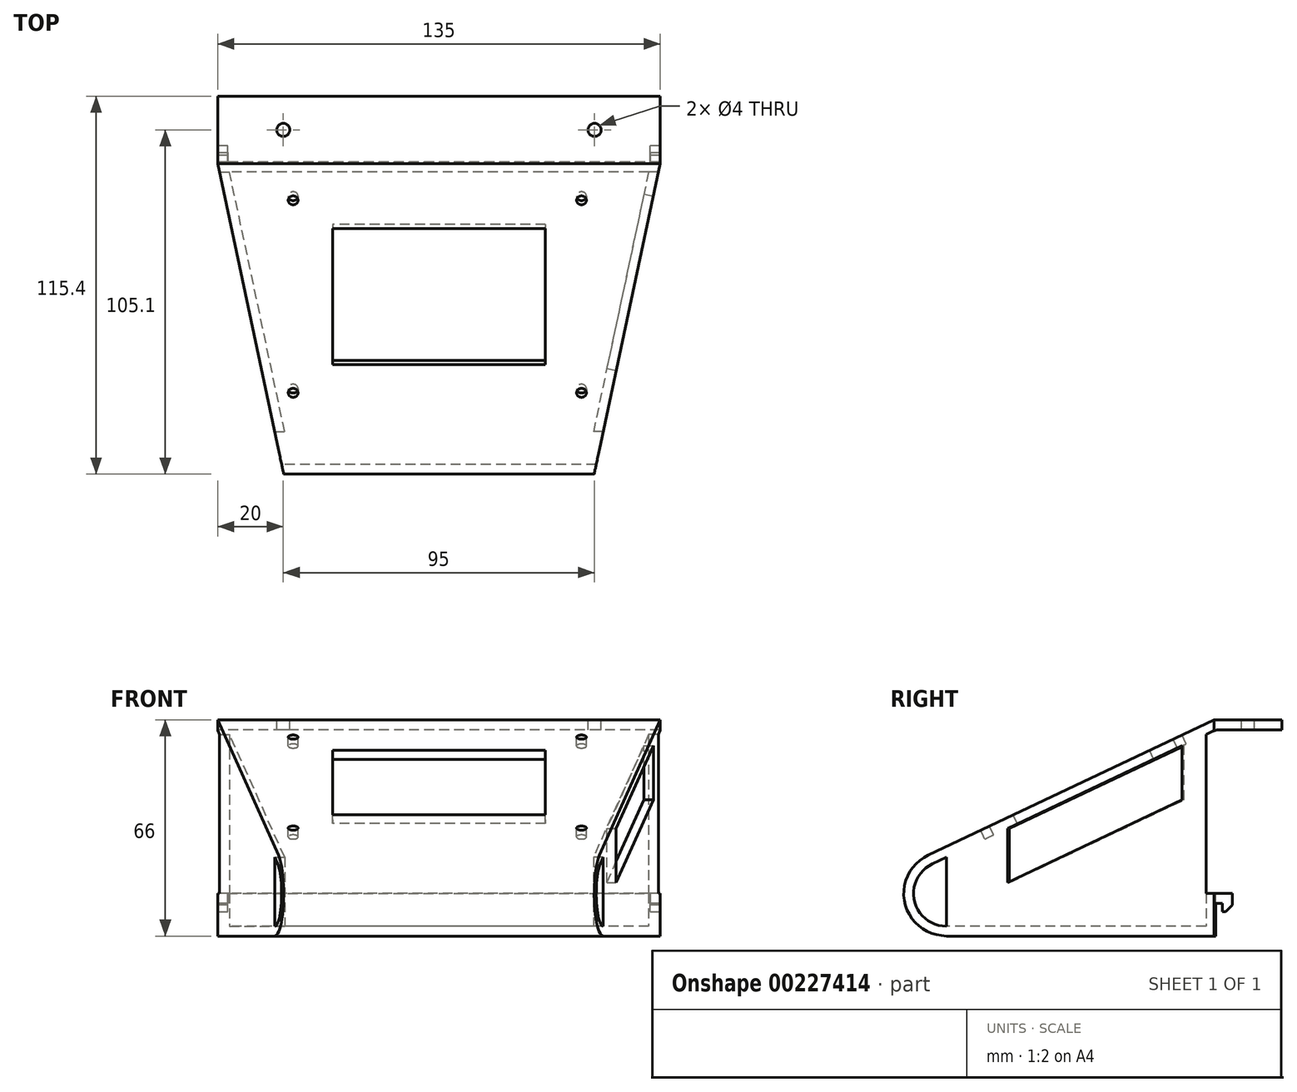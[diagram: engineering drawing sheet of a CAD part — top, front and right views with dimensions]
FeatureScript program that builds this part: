
annotation { "Feature Type Name" : "Feature", "Feature Type Description" : "" }
export const myFeature = defineFeature(function(context is Context, id is Id, definition is map)
    precondition{}
    {
        {
            var Q0;
            Q0=qCreatedBy(makeId("Right.planeOp"),FACE);
            var sketch = newSketch(context, id + "F0", { "sketchPlane" : qUnion([Q0])});
            skLineSegment(sketch, "E0", {"start": v(-20, -3) * mm, "end": v(0, -3) * mm});
            skLineSegment(sketch, "E1", {"start": v(0, -3) * mm, "end": v(0, 0) * mm});
            skLineSegment(sketch, "E2", {"start": v(0, 0) * mm, "end": v(-20.67, 0) * mm});
            skLineSegment(sketch, "E3", {"start": v(-20.67, 0) * mm, "end": v(-107.95, -41.25) * mm});
            skPoint(sketch, "E4.visualSharp", {"position": v(0, 0) * mm});
            skLineSegment(sketch, "E5", {"start": v(-102.4, -66) * mm, "end": v(-20.13, -66) * mm});
            skLineSegment(sketch, "E6", {"start": v(-23.13, -63) * mm, "end": v(-102.4, -63) * mm});
            skLineSegment(sketch, "E7.trimOffspring", {"start": v(-106.67, -43.96) * mm, "end": v(-20, -3) * mm});
            skArc(sketch, "E8.filletArc", {"start": v(-107.95, -41.25) * mm, "mid": v(-115.08, -55.85) * mm, "end": v(-102.4, -66) * mm});
            skLineSegment(sketch, "E9", {"start": v(-23.13, -63) * mm, "end": v(-23.13, -53) * mm});
            skLineSegment(sketch, "E10", {"start": v(-23.13, -53) * mm, "end": v(-15.13, -53) * mm});
            skLineSegment(sketch, "E11", {"start": v(-15.13, -53) * mm, "end": v(-15.13, -58.5) * mm});
            skLineSegment(sketch, "E12", {"start": v(-15.13, -58.5) * mm, "end": v(-18.13, -58.5) * mm});
            skLineSegment(sketch, "E13", {"start": v(-18.13, -58.5) * mm, "end": v(-18.13, -56) * mm});
            skLineSegment(sketch, "E14", {"start": v(-18.13, -56) * mm, "end": v(-20.13, -56) * mm});
            skLineSegment(sketch, "E15", {"start": v(-20.13, -56) * mm, "end": v(-20.13, -66) * mm});
            skPoint(sketch, "E16.startSnap0", {"position": v(-10, -3) * mm});
            skPoint(sketch, "E16.endSnap0", {"position": v(-10, -3) * mm});
            skArc(sketch, "E17", {"start": v(-106.67, -43.96) * mm, "mid": v(-112.15, -55.19) * mm, "end": v(-102.4, -63) * mm});
            skSolve(sketch);
        }
        {
            var Q0;
            Q0=makeQuery(id+"F0.imprint","IMPRINT",FACE,{"disambiguationData":[TD([[makeQuery(id+"F0.imprint","IMPRINT",EDGE,{"derivedFrom":sQuery(id+"F0.wireOp",EDGE,"E0")}),1.0]])]});
            extrude(context, id + "F1", {"entities" : qUnion([Q0]), "depth" : 135 * mm});
        }
        {
            var Q0;
            Q0=makeQuery(id+"F1.opExtrude","SWEPT_FACE",FACE,{"disambiguationData":[OSD([sQuery(id+"F0.wireOp",EDGE,"E3")])]});
            var sketch = newSketch(context, id + "F2", { "sketchPlane" : qUnion([Q0])});
            skCircle(sketch, "E18", {"center": v(23, -31) * mm, "radius": 1.5 * mm});
            skCircle(sketch, "E19", {"center": v(111, -31) * mm, "radius": 1.5 * mm});
            skCircle(sketch, "E20", {"center": v(23, -96) * mm, "radius": 1.5 * mm});
            skCircle(sketch, "E21", {"center": v(111, -96) * mm, "radius": 1.5 * mm});
            skLineSegment(sketch, "E22.bottom", {"start": v(35, -86.5) * mm, "end": v(100, -86.5) * mm});
            skLineSegment(sketch, "E22.top", {"start": v(35, -40.5) * mm, "end": v(100, -40.5) * mm});
            skLineSegment(sketch, "E22.left", {"start": v(35, -86.5) * mm, "end": v(35, -40.5) * mm});
            skLineSegment(sketch, "E22.right", {"start": v(100, -86.5) * mm, "end": v(100, -40.5) * mm});
            skSolve(sketch);
        }
        {
            var Q0;
            Q0=makeQuery(id+"F2.imprint","IMPRINT",FACE,{"disambiguationData":[TD([[makeQuery(id+"F2.imprint","IMPRINT",EDGE,{"derivedFrom":sQuery(id+"F2.wireOp",EDGE,"E18")}),1.0]])]});
            var Q1;
            Q1=makeQuery(id+"F2.imprint","IMPRINT",FACE,{"disambiguationData":[TD([[makeQuery(id+"F2.imprint","IMPRINT",EDGE,{"derivedFrom":sQuery(id+"F2.wireOp",EDGE,"E19")}),1.0]])]});
            var Q2;
            Q2=makeQuery(id+"F2.imprint","IMPRINT",FACE,{"disambiguationData":[TD([[makeQuery(id+"F2.imprint","IMPRINT",EDGE,{"derivedFrom":sQuery(id+"F2.wireOp",EDGE,"1yFHw2Ed-GRUs-Yyfu-eWYc-71vGHyV2RhUZ.bottom")}),-1.0]])]});
            var Q3;
            Q3=makeQuery(id+"F2.imprint","IMPRINT",FACE,{"disambiguationData":[TD([[makeQuery(id+"F2.imprint","IMPRINT",EDGE,{"derivedFrom":sQuery(id+"F2.wireOp",EDGE,"E21")}),1.0]])]});
            var Q4;
            Q4=makeQuery(id+"F2.imprint","IMPRINT",FACE,{"disambiguationData":[TD([[makeQuery(id+"F2.imprint","IMPRINT",EDGE,{"derivedFrom":sQuery(id+"F2.wireOp",EDGE,"E20")}),1.0]])]});
            var Q5;
            Q5=makeQuery(id+"F2.imprint","IMPRINT",FACE,{"disambiguationData":[TD([[makeQuery(id+"F2.imprint","IMPRINT",EDGE,{"derivedFrom":sQuery(id+"F2.wireOp",EDGE,"E22.bottom")}),1.0]])]});
            extrude(context, id + "F3", {"entities" : qUnion([Q0, Q1, Q2, Q3, Q4, Q5]), "operationType" : NewBodyOperationType.REMOVE, "endBound" : BoundingType.UP_TO_NEXT, "oppositeDirection" : true, "depth" : 25 * mm});
        }
        {
            var Q0;
            Q0=makeQuery(id+"F1.opExtrude","SWEPT_FACE",FACE,{"disambiguationData":[OSD([sQuery(id+"F0.wireOp",EDGE,"E2")])]});
            var sketch = newSketch(context, id + "F4", { "sketchPlane" : qUnion([Q0])});
            skCircle(sketch, "E23", {"center": v(20, -10.3) * mm, "radius": 2 * mm});
            skCircle(sketch, "E24", {"center": v(115, -10.3) * mm, "radius": 2 * mm});
            skSolve(sketch);
        }
        {
            var Q0;
            Q0=makeQuery(id+"F4.imprint","IMPRINT",FACE,{"disambiguationData":[TD([[makeQuery(id+"F4.imprint","IMPRINT",EDGE,{"derivedFrom":sQuery(id+"F4.wireOp",EDGE,"E23")}),1.0]])]});
            var Q1;
            Q1=makeQuery(id+"F4.imprint","IMPRINT",FACE,{"disambiguationData":[TD([[makeQuery(id+"F4.imprint","IMPRINT",EDGE,{"derivedFrom":sQuery(id+"F4.wireOp",EDGE,"E24")}),1.0]])]});
            extrude(context, id + "F5", {"entities" : qUnion([Q0, Q1]), "operationType" : NewBodyOperationType.REMOVE, "endBound" : BoundingType.UP_TO_NEXT, "oppositeDirection" : true, "depth" : 25 * mm});
        }
        {
            var Q0;
            Q0=makeQuery(id+"F1.opExtrude","SWEPT_EDGE",EDGE,{"disambiguationData":[OSD([sQuery(id+"F0.wireOp",EDGE,"E11"),sQuery(id+"F0.wireOp",EDGE,"E12")])]});
            chamfer(context, id + "F6", {"entities" : qUnion([Q0]), "width" : 2 * mm, "tangentPropagation" : true});
        }
        {
            var Q0;
            Q0=makeQuery(id+"F1.opExtrude","SWEPT_EDGE",EDGE,{"disambiguationData":[OSD([sQuery(id+"F0.wireOp",EDGE,"E0"),sQuery(id+"F0.wireOp",EDGE,"E7.trimOffspring")])]});
            fillet(context, id + "F7", {"entities" : qUnion([Q0]), "radius" : 5 * mm, "tangentPropagation" : true, "allowEdgeOverflow" : false});
        }
        {
            var Q0;
            Q0=qCreatedBy(makeId("Top.planeOp"),FACE);
            cPlane(context, id + "F8", {"entities" : qUnion([Q0]), "cplaneType" : CPlaneType.OFFSET, "offset" : 50 * mm, "width" : 150 * mm, "height" : 150 * mm});
        }
        {
            var Q0;
            Q0=qCreatedBy(id+"F8.planeOp",FACE);
            var sketch = newSketch(context, id + "F9", { "sketchPlane" : qUnion([Q0])});
            skLineSegment(sketch, "E25", {"start": v(135, -20.67) * mm, "end": v(108.43, -145.67) * mm});
            skLineSegment(sketch, "E26", {"start": v(0, -20.67) * mm, "end": v(26.57, -145.67) * mm});
            skLineSegment(sketch, "E27", {"start": v(135, -20.67) * mm, "end": v(135, -145.67) * mm});
            skLineSegment(sketch, "E28", {"start": v(135, -145.67) * mm, "end": v(108.43, -145.67) * mm});
            skLineSegment(sketch, "E29", {"start": v(0, -20.67) * mm, "end": v(0, -145.67) * mm});
            skLineSegment(sketch, "E30", {"start": v(0, -145.67) * mm, "end": v(26.57, -145.67) * mm});
            skSolve(sketch);
        }
        {
            var Q0;
            Q0=makeQuery(id+"F9.imprint","IMPRINT",FACE,{"disambiguationData":[TD([[makeQuery(id+"F9.imprint","IMPRINT",EDGE,{"derivedFrom":sQuery(id+"F9.wireOp",EDGE,"E26")}),-1.0]])]});
            var Q1;
            Q1=makeQuery(id+"F9.imprint","IMPRINT",FACE,{"disambiguationData":[TD([[makeQuery(id+"F9.imprint","IMPRINT",EDGE,{"derivedFrom":sQuery(id+"F9.wireOp",EDGE,"E25")}),1.0]])]});
            var Q2;
            Q2=makeQuery(id+"F1.opExtrude","SWEPT_FACE",FACE,{"disambiguationData":[OSD([sQuery(id+"F0.wireOp",EDGE,"E5")])]});
            extrude(context, id + "F10", {"entities" : qUnion([Q0, Q1]), "operationType" : NewBodyOperationType.REMOVE, "endBound" : BoundingType.UP_TO_SURFACE, "oppositeDirection" : true, "endBoundEntityFace" : qUnion([Q2]), "depth" : 25 * mm});
        }
        {
            var Q0;
            Q0=makeQuery(id+"F1.opExtrude","SWEPT_FACE",FACE,{"disambiguationData":[OSD([sQuery(id+"F0.wireOp",EDGE,"E6")])]});
            var sketch = newSketch(context, id + "F11", { "sketchPlane" : qUnion([Q0])});
            skLineSegment(sketch, "E31.0", {"start": v(117.63, -102.4) * mm, "end": v(134.48, -23.13) * mm});
            skLineSegment(sketch, "E32", {"start": v(134.48, -23.13) * mm, "end": v(131.48, -23.13) * mm});
            skLineSegment(sketch, "E33", {"start": v(131.48, -23.13) * mm, "end": v(114.63, -102.4) * mm});
            skLineSegment(sketch, "E34", {"start": v(114.63, -102.4) * mm, "end": v(117.63, -102.4) * mm});
            skSolve(sketch);
        }
        {
            var Q0;
            Q0=makeQuery(id+"F11.imprint","IMPRINT",FACE,{"disambiguationData":[TD([[makeQuery(id+"F11.imprint","IMPRINT",EDGE,{"derivedFrom":sQuery(id+"F11.wireOp",EDGE,"E31.0")}),1.0]])]});
            extrude(context, id + "F12", {"entities" : qUnion([Q0]), "operationType" : NewBodyOperationType.ADD, "endBound" : BoundingType.UP_TO_NEXT, "depth" : 25 * mm});
        }
        {
            var Q0;
            Q0=qCreatedBy(makeId("Right.planeOp"),FACE);
            cPlane(context, id + "F13", {"entities" : qUnion([Q0]), "cplaneType" : CPlaneType.OFFSET, "offset" : (135 / 2) * mm, "width" : 150 * mm, "height" : 150 * mm});
        }
        {
            var Q0;
            Q0=qCreatedBy(id+"F13.planeOp",FACE);
            var sketch = newSketch(context, id + "F14", { "sketchPlane" : qUnion([Q0])});
            skLineSegment(sketch, "E35.0", {"start": v(-20.13, -53) * mm, "end": v(-15.13, -53) * mm});
            skLineSegment(sketch, "E36.0", {"start": v(-15.13, -53) * mm, "end": v(-15.13, -56.5) * mm});
            skLineSegment(sketch, "E37.0", {"start": v(-17.13, -58.5) * mm, "end": v(-15.13, -56.5) * mm});
            skLineSegment(sketch, "E38.0", {"start": v(-17.13, -58.5) * mm, "end": v(-18.13, -58.5) * mm});
            skLineSegment(sketch, "E39.0", {"start": v(-18.13, -58.5) * mm, "end": v(-18.13, -56) * mm});
            skLineSegment(sketch, "E40.0", {"start": v(-18.13, -56) * mm, "end": v(-20.13, -56) * mm});
            skLineSegment(sketch, "E41", {"start": v(-20.13, -56) * mm, "end": v(-20.13, -53) * mm});
            skPoint(sketch, "E42.orphan", {"position": v(-20.67, -53) * mm});
            skSolve(sketch);
        }
        {
            var Q0;
            Q0=makeQuery(id+"F14.imprint","IMPRINT",FACE,{"disambiguationData":[TD([[makeQuery(id+"F14.imprint","IMPRINT",EDGE,{"derivedFrom":sQuery(id+"F14.wireOp",EDGE,"E35.0")}),-1.0]])]});
            extrude(context, id + "F15", {"entities" : qUnion([Q0]), "operationType" : NewBodyOperationType.REMOVE, "oppositeDirection" : true, "depth" : (129 / 2) * mm, "hasSecondDirection" : true, "secondDirectionOppositeDirection" : false, "secondDirectionDepth" : (129 / 2) * mm});
        }
        {
            var Q0;
            Q0=makeQuery(id+"F1.opExtrude","SWEPT_FACE",FACE,{"disambiguationData":[OSD([sQuery(id+"F0.wireOp",EDGE,"E6")])]});
            var sketch = newSketch(context, id + "F16", { "sketchPlane" : qUnion([Q0])});
            skLineSegment(sketch, "E43.0", {"start": v(17.37, -102.4) * mm, "end": v(0.52, -23.13) * mm});
            skLineSegment(sketch, "E44", {"start": v(0.52, -23.13) * mm, "end": v(3.59, -23.13) * mm});
            skLineSegment(sketch, "E45", {"start": v(3.59, -23.13) * mm, "end": v(20.44, -102.4) * mm});
            skLineSegment(sketch, "E46", {"start": v(20.44, -102.4) * mm, "end": v(17.37, -102.4) * mm});
            skSolve(sketch);
        }
        {
            var Q0;
            Q0=makeQuery(id+"F16.imprint","IMPRINT",FACE,{"disambiguationData":[TD([[makeQuery(id+"F16.imprint","IMPRINT",EDGE,{"derivedFrom":sQuery(id+"F16.wireOp",EDGE,"E43.0")}),-1.0]])]});
            var Q1;
            Q1=makeQuery(id+"F1.opExtrude","SWEPT_FACE",FACE,{"disambiguationData":[OSD([sQuery(id+"F0.wireOp",EDGE,"E3")])]});
            extrude(context, id + "F17", {"entities" : qUnion([Q0]), "operationType" : NewBodyOperationType.ADD, "endBound" : BoundingType.UP_TO_SURFACE, "endBoundEntityFace" : qUnion([Q1]), "depth" : 25 * mm});
        }
        {
            var Q0;
            Q0=makeQuery(id+"F12.boolean.opBoolean","MERGE",FACE,{"derivedFrom":[makeQuery(id+"F10.boolean.opBoolean","COPY",FACE,{"derivedFrom":makeQuery(id+"F10.opExtrude","SWEPT_FACE",FACE,{"disambiguationData":[OSD([sQuery(id+"F9.wireOp",EDGE,"E25")])]})}),makeQuery(id+"F12.opExtrude","SWEPT_FACE",FACE,{"disambiguationData":[OSD([sQuery(id+"F11.wireOp",EDGE,"E31.0")])]})]});
            var sketch = newSketch(context, id + "F18", { "sketchPlane" : qUnion([Q0])});
            skLineSegment(sketch, "E47", {"start": v(-56.62, -33.1) * mm, "end": v(-2.15, -7.93) * mm});
            skLineSegment(sketch, "E48", {"start": v(-2.15, -7.93) * mm, "end": v(-2.15, -24.45) * mm});
            skLineSegment(sketch, "E49", {"start": v(-2.15, -24.45) * mm, "end": v(-56.62, -49.63) * mm});
            skLineSegment(sketch, "E50", {"start": v(-56.62, -33.1) * mm, "end": v(-56.62, -49.63) * mm});
            skSolve(sketch);
        }
        {
            var Q0;
            {var subQ0=sQuery(id+"F18.wireOp",EDGE,"E49");Q0=makeQuery(id+"F18.imprint","IMPRINT",FACE,{"disambiguationData":[TD([[makeQuery(id+"F18.imprint","IMPRINT",EDGE,{"derivedFrom":subQ0}),-1.0]])]});}
            extrude(context, id + "F19", {"entities" : qUnion([Q0]), "operationType" : NewBodyOperationType.REMOVE, "endBound" : BoundingType.UP_TO_NEXT, "oppositeDirection" : true, "depth" : 25 * mm});
        }
    });
